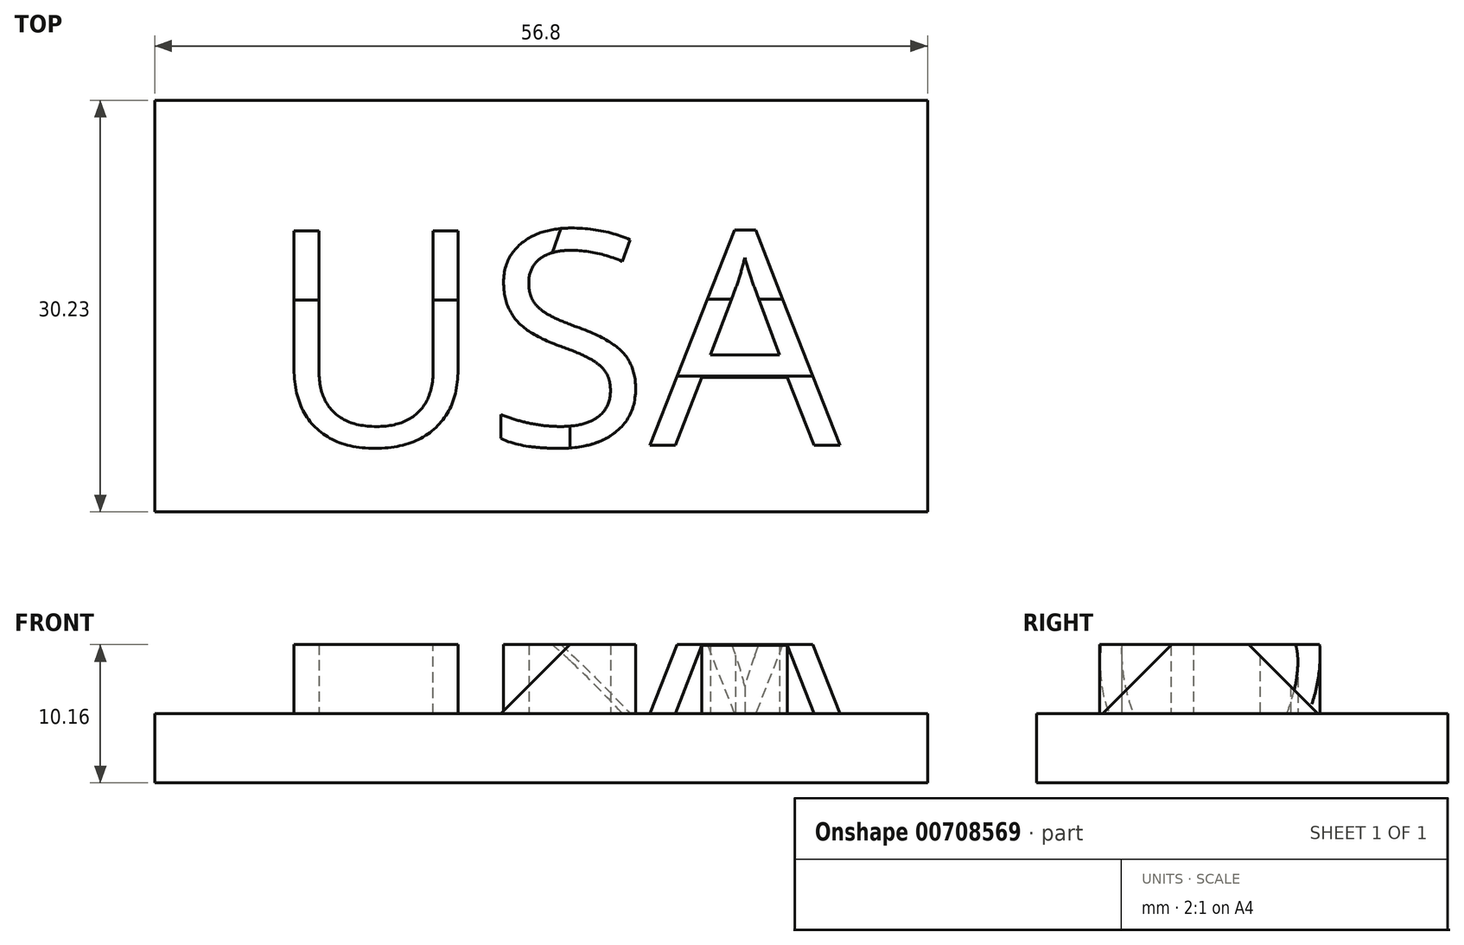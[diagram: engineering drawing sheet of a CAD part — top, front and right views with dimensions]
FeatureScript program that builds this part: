
annotation { "Feature Type Name" : "Feature", "Feature Type Description" : "" }
export const myFeature = defineFeature(function(context is Context, id is Id, definition is map)
    precondition{}
    {
        {
            var Q0;
            Q0=qCreatedBy(makeId("Top.planeOp"),FACE);
            var sketch = newSketch(context, id + "F0", { "sketchPlane" : qUnion([Q0])});
            skLineSegment(sketch, "E0.bottom", {"start": v(-53.6, 36.8) * mm, "end": v(3.2, 36.8) * mm});
            skLineSegment(sketch, "E0.top", {"start": v(-53.6, 6.57) * mm, "end": v(3.2, 6.57) * mm});
            skLineSegment(sketch, "E0.left", {"start": v(-53.6, 36.8) * mm, "end": v(-53.6, 6.57) * mm});
            skLineSegment(sketch, "E0.right", {"start": v(3.2, 36.8) * mm, "end": v(3.2, 6.57) * mm});
            skSolve(sketch);
        }
        {
            var Q0;
            Q0=makeQuery(id+"F0.imprint","IMPRINT",FACE,{"disambiguationData":[TD([[makeQuery(id+"F0.imprint","IMPRINT",EDGE,{"derivedFrom":sQuery(id+"F0.wireOp",EDGE,"E0.bottom")}),-1.0]])]});
            extrude(context, id + "F1", {"entities" : qUnion([Q0]), "depth" : 5.08 * mm, "offsetDistance" : 25.4 * mm});
        }
        {
            var Q0;
            Q0=makeQuery(id+"F1.opExtrude","CAP_FACE",FACE,{"disambiguationData":[OSD([sQuery(id+"F0.wireOp",EDGE,"E0.bottom"),sQuery(id+"F0.wireOp",EDGE,"E0.top"),sQuery(id+"F0.wireOp",EDGE,"E0.left"),sQuery(id+"F0.wireOp",EDGE,"E0.right")])],"isStart":false});
            var sketch = newSketch(context, id + "F2", { "sketchPlane" : qUnion([Q0])});
            skText(sketch, "E1", { "text": "USA", "fontName": "OpenSans-Regular.ttf"});
            const initialGuessF2  = {"E1": [-0.04535, 0.01145, 1, 0, 0.01588]};
            skSetInitialGuess(sketch, initialGuessF2);
            skSolve(sketch);
        }
        {
            var Q0;
            Q0 = qSketchRegion(id + "F2", true);
            extrude(context, id + "F3", {"entities" : qUnion([Q0]), "operationType" : NewBodyOperationType.ADD, "depth" : 5.08 * mm, "offsetDistance" : 25.4 * mm});
        }
        {
            var Q0;
            Q0=makeQuery(id+"F3.opExtrude","CAP_EDGE",EDGE,{"disambiguationData":[OSD([sQuery(id+"F2.wireOp",EDGE,"E1.sketch_text.stroke-6")])],"isStart":false});
            var Q1;
            Q1=makeQuery(id+"F3.opExtrude","CAP_EDGE",EDGE,{"disambiguationData":[OSD([sQuery(id+"F2.wireOp",EDGE,"E1.sketch_text.stroke-13")])],"isStart":false});
            var Q2;
            Q2=makeQuery(id+"F3.opExtrude","CAP_EDGE",EDGE,{"disambiguationData":[OSD([sQuery(id+"F2.wireOp",EDGE,"E1.sketch_text.stroke-17")])],"isStart":false});
            var Q3;
            Q3=makeQuery(id+"F3.opExtrude","CAP_EDGE",EDGE,{"disambiguationData":[OSD([sQuery(id+"F2.wireOp",EDGE,"E1.sketch_text.stroke-30")])],"isStart":false});
            var Q4;
            Q4=makeQuery(id+"F3.opExtrude","CAP_EDGE",EDGE,{"disambiguationData":[OSD([sQuery(id+"F2.wireOp",EDGE,"E1.sketch_text.stroke-42")])],"isStart":false});
            var Q5;
            Q5=makeQuery(id+"F3.opExtrude","CAP_EDGE",EDGE,{"disambiguationData":[OSD([sQuery(id+"F2.wireOp",EDGE,"E1.sketch_text.stroke-44")])],"isStart":false});
            chamfer(context, id + "F4", {"entities" : qUnion([Q0, Q1, Q2, Q3, Q4, Q5]), "width" : 5.08 * mm, "tangentPropagation" : true});
        }
    });
